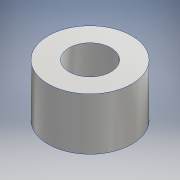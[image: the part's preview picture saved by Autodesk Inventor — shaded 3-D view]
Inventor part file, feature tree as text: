
AUTODESK INVENTOR PART (.ipt)
format: ipt  version: 2016 (Build 200138000, 138)  size: 98,304 bytes
history: native  units: mm
features: extrude x2, sketch x2, other x1
ambient origin geometry x8: Origin, YZ Plane, XZ Plane, XY Plane, X Axis, Y Axis, Z Axis, Center Point
bodies: Body1 (feature_tree)
feature tree (5):
  other  "ソリッド1"
  extrude  "押し出し1"  Depth=8.0mm
  extrude  "押し出し2"  Depth=5.0mm TaperAngle=0.0deg
  sketch  "スケッチ1"
  sketch  "スケッチ2"
